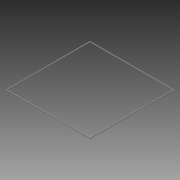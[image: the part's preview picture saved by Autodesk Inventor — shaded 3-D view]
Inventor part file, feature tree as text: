
AUTODESK INVENTOR PART (.ipt)
format: ipt  version: 2015 SP1 (Build 190203100, 203)  size: 75,264 bytes
history: native  units: mm
features: extrude x1, sketch x1
ambient origin geometry x8: Origin, YZ Plane, XZ Plane, XY Plane, X Axis, Y Axis, Z Axis, Center Point
bodies: Solid1 (feature_tree)
feature tree (2):
  extrude  "Extrusion1"  Depth=360.0mm
  sketch  "Sketch1"  dims[d0=360.0mm d1=360.0mm d2=365.0mm d3=365.0mm d4=2.6mm d5=0.0mm]
